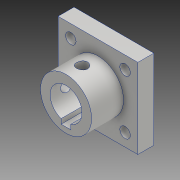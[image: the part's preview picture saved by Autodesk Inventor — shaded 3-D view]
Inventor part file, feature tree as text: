
AUTODESK INVENTOR PART (.ipt)
format: ipt  version: 2020 (Build 240168000, 168)  size: 220,672 bytes
history: native  units: mm
features: extrude x5, sketch x5, other x1
ambient origin geometry x8: Origin, YZ Plane, XZ Plane, XY Plane, X Axis, Y Axis, Z Axis, Center Point
bodies: Solid1 (feature_tree)
feature tree (11):
  extrude  "Extrusion1"  Depth=20.0mm
  extrude  "Extrusion4"  Depth=30.0mm
  extrude  "Extrusion5"  Depth=30.0mm TaperAngle=0.0deg
  extrude  "Extrusion6"  Depth=10.0mm
  other  "Spur Gear Teeth7"
  extrude  "Extrusion7"  Depth=6.1mm
  sketch  "Sketch1"  dims[d0=20.0mm d1=32.0mm]
  sketch  "Sketch4"  dims[d2=30.0mm d3=0.0mm d13=6.9mm]
  sketch  "Sketch5"  dims[d14=10.0mm d15=30.0mm d16=0.0mm]
  sketch  "Sketch6"  dims[d17=6.9mm d18=10.0mm]
  sketch  "Sketch9"  dims[d19=30.0mm d20=0.0mm d21=6.1mm d22=3.05mm d23=0.0mm d24=0.0mm d25=50.0mm d26=50.0mm d27=25.0mm d28=25.0mm d29=6.53mm d30=8.0mm d31=8.0mm d32=8.0mm d33=8.0mm d35=8.0mm d36=8.0mm d37=8.0mm d38=8.0mm d39=10.0mm d40=0.0mm]
